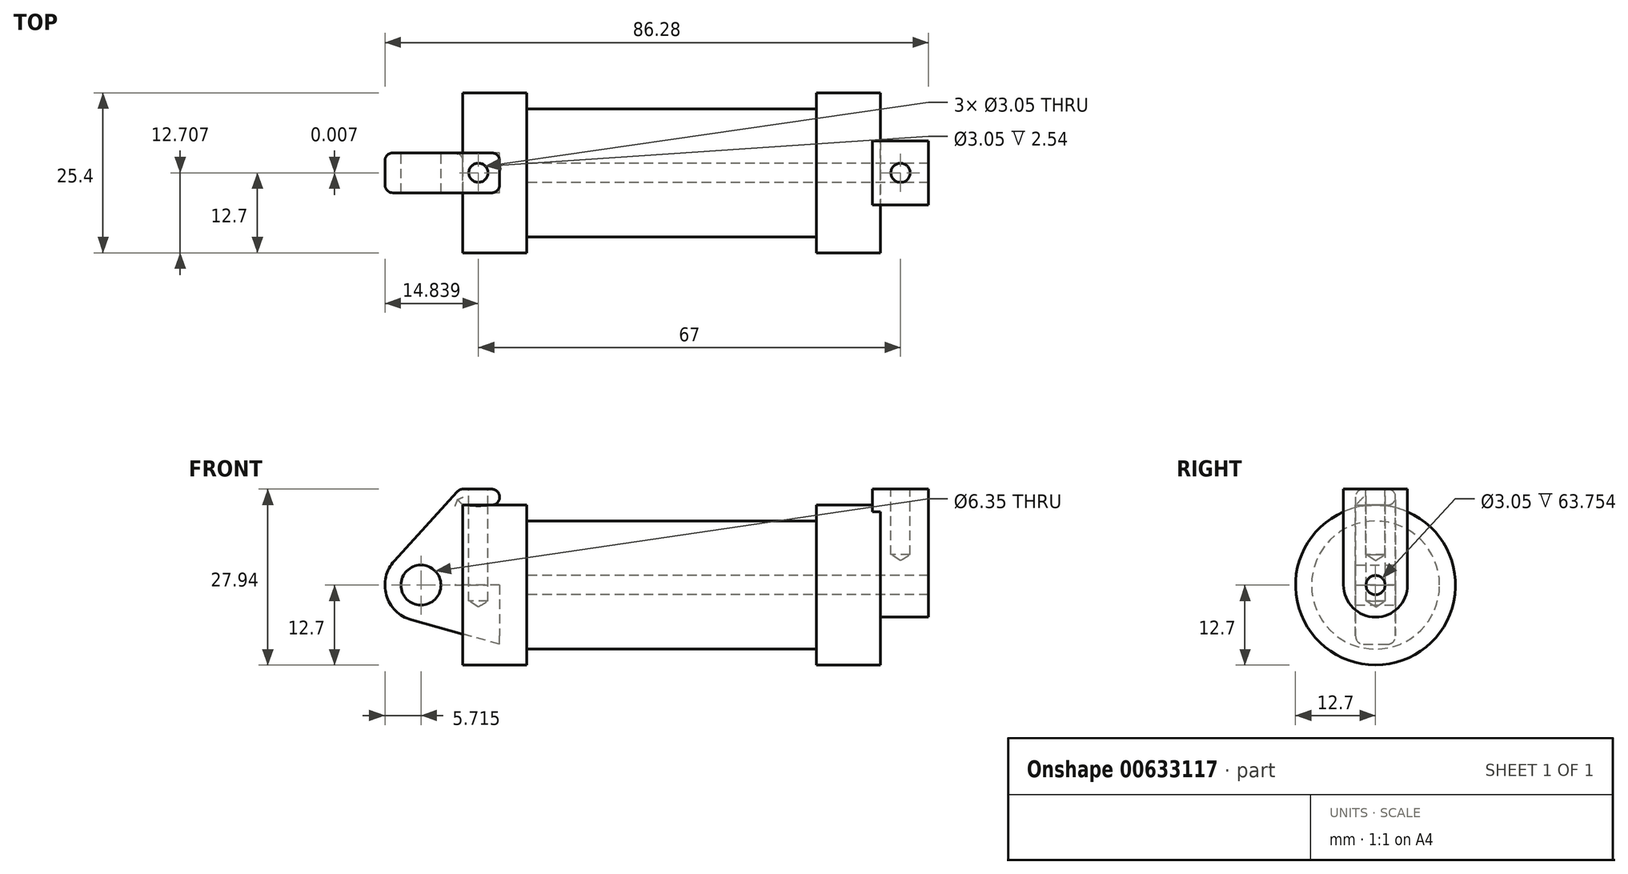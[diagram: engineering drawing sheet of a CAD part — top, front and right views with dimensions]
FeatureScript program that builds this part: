
annotation { "Feature Type Name" : "Feature", "Feature Type Description" : "" }
export const myFeature = defineFeature(function(context is Context, id is Id, definition is map)
    precondition{}
    {
        {
            var Q0;
            Q0=qCreatedBy(makeId("Front.planeOp"),FACE);
            var sketch = newSketch(context, id + "F0", { "sketchPlane" : qUnion([Q0])});
            skLineSegment(sketch, "E0", {"start": v(0, 0) * mm, "end": v(0, 12.7) * mm});
            skLineSegment(sketch, "E1", {"start": v(0, 12.7) * mm, "end": v(10.16, 12.7) * mm});
            skLineSegment(sketch, "E2", {"start": v(10.16, 12.7) * mm, "end": v(10.16, 10.16) * mm});
            skLineSegment(sketch, "E3", {"start": v(10.16, 10.16) * mm, "end": v(56.13, 10.16) * mm});
            skLineSegment(sketch, "E4", {"start": v(56.13, 10.16) * mm, "end": v(56.13, 12.7) * mm});
            skLineSegment(sketch, "E5", {"start": v(56.13, 12.7) * mm, "end": v(66.3, 12.7) * mm});
            skLineSegment(sketch, "E6", {"start": v(66.3, 12.7) * mm, "end": v(66.3, 0) * mm});
            skLineSegment(sketch, "E7", {"start": v(66.3, 0) * mm, "end": v(0, 0) * mm});
            skLineSegment(sketch, "E8", {"start": v(5.84, 15.24) * mm, "end": v(-0.5, 15.24) * mm});
            skLineSegment(sketch, "E9", {"start": v(-0.5, 15.24) * mm, "end": v(-10.88, 3.85) * mm});
            skLineSegment(sketch, "E10", {"start": v(0, 0) * mm, "end": v(-6.65, 0) * mm});
            skCircle(sketch, "E11", {"center": v(-6.65, 0) * mm, "radius": 5.72 * mm});
            skCircle(sketch, "E12", {"center": v(-6.65, 0) * mm, "radius": 3.18 * mm});
            skLineSegment(sketch, "E13", {"start": v(5.84, 15.24) * mm, "end": v(5.84, -9.4) * mm});
            skLineSegment(sketch, "E14", {"start": v(5.84, -9.4) * mm, "end": v(-8.18, -5.5) * mm});
            skSolve(sketch);
        }
        {
            var Q0;
            {var subQ0=sQuery(id+"F0.wireOp",EDGE,"E0");Q0=makeQuery(id+"F0.imprint","IMPRINT",FACE,{"disambiguationData":[TD([[makeQuery(id+"F0.imprint","IMPRINT",EDGE,{"derivedFrom":subQ0}),-1.0]])]});}
            var Q1;
            {var subQ0=sQuery(id+"F0.wireOp",EDGE,"E2");Q1=makeQuery(id+"F0.imprint","IMPRINT",FACE,{"disambiguationData":[TD([[makeQuery(id+"F0.imprint","IMPRINT",EDGE,{"derivedFrom":subQ0}),-1.0]])]});}
            var Q2;
            Q2=sQuery(id+"F0.wireOp",EDGE,"E7");
            revolve(context, id + "F1", {"entities" : qUnion([Q0, Q1]), "axis" : qUnion([Q2]), "revolveType" : RevolveType.FULL});
        }
        {
            var Q0;
            {var subQ0=sQuery(id+"F0.wireOp",EDGE,"E14");Q0=makeQuery(id+"F0.imprint","IMPRINT",FACE,{"disambiguationData":[TD([[makeQuery(id+"F0.imprint","IMPRINT",EDGE,{"derivedFrom":subQ0}),-1.0]])]});}
            var Q1;
            {var subQ1=sQuery(id+"F0.wireOp",EDGE,"E0");Q1=makeQuery(id+"F0.imprint","IMPRINT",FACE,{"disambiguationData":[TD([[makeQuery(id+"F0.imprint","IMPRINT",EDGE,{"derivedFrom":subQ1}),1.0]])]});}
            var Q2;
            {var subQ5=sQuery(id+"F0.wireOp",EDGE,"E12");Q2=makeQuery(id+"F0.imprint","IMPRINT",FACE,{"disambiguationData":[TD([[makeQuery(id+"F0.imprint","IMPRINT",EDGE,{"derivedFrom":subQ5}),-1.0]])]});}
            extrude(context, id + "F2", {"entities" : qUnion([Q0, Q1, Q2]), "endBound" : BoundingType.SYMMETRIC, "depth" : 6.35 * mm, "offsetDistance" : 25.4 * mm});
        }
        {
            var Q0;
            Q0=makeQuery(id+"F1.opRevolve","SWEPT_FACE",FACE,{"disambiguationData":[OSD([sQuery(id+"F0.wireOp",EDGE,"E6")])]});
            var sketch = newSketch(context, id + "F3", { "sketchPlane" : qUnion([Q0])});
            skCircle(sketch, "E15", {"center": v(0, 0) * mm, "radius": 1.52 * mm});
            skCircle(sketch, "E16", {"center": v(0, 0) * mm, "radius": 5.08 * mm});
            skLineSegment(sketch, "E17", {"start": v(-5.08, 0) * mm, "end": v(-5.08, 15.24) * mm});
            skLineSegment(sketch, "E18", {"start": v(5.08, 0) * mm, "end": v(5.08, 15.24) * mm});
            skLineSegment(sketch, "E19", {"start": v(5.08, 15.24) * mm, "end": v(-5.08, 15.24) * mm});
            skSolve(sketch);
        }
        {
            var Q0;
            Q0=makeQuery(id+"F3.imprint","IMPRINT",FACE,{"disambiguationData":[TD([[makeQuery(id+"F3.imprint","IMPRINT",EDGE,{"derivedFrom":sQuery(id+"F3.wireOp",EDGE,"E15")}),-1.0]])]});
            var Q1;
            {var subQ0=sQuery(id+"F3.wireOp",EDGE,"E17");var subQ1=sQuery(id+"F3.wireOp",EDGE,"E16");var subQ2=makeQuery(id+"F3.imprint","INTERSECT",VERTEX,{"derivedFrom":[subQ1,subQ0]});Q1=makeQuery(id+"F3.imprint","IMPRINT",FACE,{"disambiguationData":[TD([[makeQuery(id+"F3.imprint","IMPRINT",EDGE,{"disambiguationData":[TD([[subQ2,1.0]])],"derivedFrom":subQ1}),-1.0]])]});}
            var Q2;
            {var subQ0=sQuery(id+"F3.wireOp",EDGE,"E19");Q2=makeQuery(id+"F3.imprint","IMPRINT",FACE,{"disambiguationData":[TD([[makeQuery(id+"F3.imprint","IMPRINT",EDGE,{"derivedFrom":subQ0}),1.0]])]});}
            extrude(context, id + "F4", {"entities" : qUnion([Q0, Q1, Q2]), "operationType" : NewBodyOperationType.ADD, "depth" : 7.62 * mm, "offsetDistance" : 25.4 * mm, "hasSecondDirection" : true, "secondDirectionOppositeDirection" : true, "secondDirectionDepth" : 1.27 * mm});
        }
        {
            var Q0;
            Q0=makeQuery(id+"F4.boolean.opBoolean","SPLIT",FACE,{"disambiguationData":[TD([makeQuery(id+"F4.opExtrude","SWEPT_FACE",FACE,{"disambiguationData":[OSD([sQuery(id+"F3.wireOp",EDGE,"E15")])]})])],"derivedFrom":makeQuery(id+"F1.opRevolve","SWEPT_FACE",FACE,{"disambiguationData":[OSD([sQuery(id+"F0.wireOp",EDGE,"E6")])]})});
            var Q1;
            Q1=makeQuery(id+"F1.opRevolve","SWEPT_FACE",FACE,{"disambiguationData":[OSD([sQuery(id+"F0.wireOp",EDGE,"E2")])]});
            extrude(context, id + "F5", {"entities" : qUnion([Q0]), "operationType" : NewBodyOperationType.REMOVE, "endBound" : BoundingType.UP_TO_SURFACE, "oppositeDirection" : true, "depth" : 25.4 * mm, "endBoundEntityFace" : qUnion([Q1]), "offsetDistance" : 25.4 * mm});
        }
        {
            var Q0;
            Q0=makeQuery(id+"F4.opExtrude","SWEPT_FACE",FACE,{"disambiguationData":[OSD([sQuery(id+"F3.wireOp",EDGE,"E19")])]});
            var sketch = newSketch(context, id + "F6", { "sketchPlane" : qUnion([Q0])});
            skCircle(sketch, "E20", {"center": v(69.47, 0) * mm, "radius": 1.52 * mm});
            skPoint(sketch, "E20.centerSnap0", {"position": v(69.47, 5.08) * mm});
            skPoint(sketch, "E20.centerSnap1", {"position": v(65.02, 0) * mm});
            skSolve(sketch);
        }
        {
            var Q0;
            Q0=makeQuery(id+"F2.opExtrude","SWEPT_FACE",FACE,{"disambiguationData":[OSD([sQuery(id+"F0.wireOp",EDGE,"E8")])]});
            var sketch = newSketch(context, id + "F7", { "sketchPlane" : qUnion([Q0])});
            skCircle(sketch, "E21", {"center": v(2.47, 0) * mm, "radius": 1.52 * mm});
            skSolve(sketch);
        }
        {
            var Q0;
            Q0=sQuery(id+"F7.wireOp",VERTEX,"E21.center");
            var Q1;
            Q1=makeQuery(id+"F1.opRevolve","SWEPT_BODY",BODY,{"disambiguationData":[OSD([sQuery(id+"F0.wireOp",EDGE,"E0"),sQuery(id+"F0.wireOp",EDGE,"E1"),sQuery(id+"F0.wireOp",EDGE,"E2"),sQuery(id+"F0.wireOp",EDGE,"E3"),sQuery(id+"F0.wireOp",EDGE,"E4"),sQuery(id+"F0.wireOp",EDGE,"E5"),sQuery(id+"F0.wireOp",EDGE,"E6"),sQuery(id+"F0.wireOp",EDGE,"E7")])]});
            var Q2;
            Q2=makeQuery(id+"F2.opExtrude","SWEPT_BODY",BODY,{"disambiguationData":[OSD([sQuery(id+"F0.wireOp",EDGE,"E0"),sQuery(id+"F0.wireOp",EDGE,"E1"),sQuery(id+"F0.wireOp",EDGE,"E7"),sQuery(id+"F0.wireOp",EDGE,"E8"),sQuery(id+"F0.wireOp",EDGE,"E9"),sQuery(id+"F0.wireOp",EDGE,"E11"),sQuery(id+"F0.wireOp",EDGE,"E12"),sQuery(id+"F0.wireOp",EDGE,"E13"),sQuery(id+"F0.wireOp",EDGE,"E14")])]});
            hole(context, id + "F8", {"style" : HoleStyle.SIMPLE, "endStyle" : HoleEndStyle.BLIND, "holeDiameter" : 3.05 * mm, "majorDiameter" : 6.35 * mm, "holeDepth" : 17.78 * mm, "isTappedThrough" : true, "tappedDepth" : 12.7 * mm, "tapClearance" : 3, "locations" : qUnion([Q0]), "scope" : qUnion([Q1, Q2])});
        }
        {
            var Q0;
            Q0=sQuery(id+"F6.wireOp",VERTEX,"E20.center");
            var Q1;
            Q1=makeQuery(id+"F1.opRevolve","SWEPT_BODY",BODY,{"disambiguationData":[OSD([sQuery(id+"F0.wireOp",EDGE,"E0"),sQuery(id+"F0.wireOp",EDGE,"E1"),sQuery(id+"F0.wireOp",EDGE,"E2"),sQuery(id+"F0.wireOp",EDGE,"E3"),sQuery(id+"F0.wireOp",EDGE,"E4"),sQuery(id+"F0.wireOp",EDGE,"E5"),sQuery(id+"F0.wireOp",EDGE,"E6"),sQuery(id+"F0.wireOp",EDGE,"E7")])]});
            hole(context, id + "F9", {"style" : HoleStyle.SIMPLE, "endStyle" : HoleEndStyle.BLIND, "holeDiameter" : 3.05 * mm, "majorDiameter" : 6.35 * mm, "holeDepth" : 10.4 * mm, "isTappedThrough" : true, "tappedDepth" : 12.7 * mm, "tapClearance" : 3, "locations" : qUnion([Q0]), "scope" : qUnion([Q1])});
        }
        {
            var Q0;
            Q0=makeQuery(id+"F1.opRevolve","SWEPT_EDGE",EDGE,{"disambiguationData":[OSD([sQuery(id+"F0.wireOp",EDGE,"E1"),sQuery(id+"F0.wireOp",EDGE,"E2")])]});
            var Q1;
            Q1=makeQuery(id+"F1.opRevolve","SWEPT_EDGE",EDGE,{"disambiguationData":[OSD([sQuery(id+"F0.wireOp",EDGE,"E0"),sQuery(id+"F0.wireOp",EDGE,"E1")])]});
            var Q2;
            Q2=makeQuery(id+"F1.opRevolve","SWEPT_FACE",FACE,{"disambiguationData":[OSD([sQuery(id+"F0.wireOp",EDGE,"E5")])]});
            var Q3;
            Q3=makeQuery(id+"F4.opExtrude","SWEPT_EDGE",EDGE,{"disambiguationData":[OSD([sQuery(id+"F3.wireOp",EDGE,"E17"),sQuery(id+"F3.wireOp",EDGE,"E19")])]});
            var Q4;
            Q4=makeQuery(id+"F4.opExtrude","CAP_EDGE",EDGE,{"disambiguationData":[OSD([sQuery(id+"F3.wireOp",EDGE,"E19")])],"isStart":false});
            var Q5;
            Q5=makeQuery(id+"F4.opExtrude","SWEPT_EDGE",EDGE,{"disambiguationData":[OSD([sQuery(id+"F3.wireOp",EDGE,"E18"),sQuery(id+"F3.wireOp",EDGE,"E19")])]});
            var Q6;
            Q6=makeQuery(id+"F4.opExtrude","CAP_EDGE",EDGE,{"disambiguationData":[OSD([sQuery(id+"F3.wireOp",EDGE,"E19")])],"isStart":true});
            var Q7;
            Q7=makeQuery(id+"F4.opExtrude","CAP_EDGE",EDGE,{"disambiguationData":[OSD([sQuery(id+"F3.wireOp",EDGE,"E17")])],"isStart":true});
            var Q8;
            Q8=makeQuery(id+"F4.opExtrude","CAP_EDGE",EDGE,{"disambiguationData":[OSD([sQuery(id+"F3.wireOp",EDGE,"E18")])],"isStart":true});
            var Q9;
            Q9=makeQuery(id+"F4.opExtrude","CAP_EDGE",EDGE,{"disambiguationData":[OSD([sQuery(id+"F3.wireOp",EDGE,"E18")])],"isStart":false});
            var Q10;
            Q10=makeQuery(id+"F4.opExtrude","CAP_EDGE",EDGE,{"disambiguationData":[OSD([sQuery(id+"F3.wireOp",EDGE,"E16")])],"isStart":false});
            var Q11;
            Q11=makeQuery(id+"F4.opExtrude","CAP_EDGE",EDGE,{"disambiguationData":[OSD([sQuery(id+"F3.wireOp",EDGE,"E17")])],"isStart":false});
            var Q12;
            Q12=makeQuery(id+"F2.opExtrude","CAP_EDGE",EDGE,{"disambiguationData":[OSD([sQuery(id+"F0.wireOp",EDGE,"E8")])],"isStart":true});
            var Q13;
            Q13=makeQuery(id+"F2.opExtrude","SWEPT_EDGE",EDGE,{"disambiguationData":[OSD([sQuery(id+"F0.wireOp",EDGE,"E8"),sQuery(id+"F0.wireOp",EDGE,"E9")])]});
            var Q14;
            Q14=makeQuery(id+"F2.opExtrude","CAP_EDGE",EDGE,{"disambiguationData":[OSD([sQuery(id+"F0.wireOp",EDGE,"E8")])],"isStart":false});
            var Q15;
            Q15=makeQuery(id+"F2.opExtrude","SWEPT_EDGE",EDGE,{"disambiguationData":[OSD([sQuery(id+"F0.wireOp",EDGE,"E8"),sQuery(id+"F0.wireOp",EDGE,"E13")])]});
            var Q16;
            {var subQ0=sQuery(id+"F0.wireOp",EDGE,"E13");Q16=makeQuery(id+"F2.opExtrude","CAP_EDGE",EDGE,{"disambiguationData":[OSD([subQ0]),TDD([makeQuery(id+"F0.imprint","IMPRINT",EDGE,{"disambiguationData":[TD([[makeQuery(id+"F0.imprint","INTERSECT",VERTEX,{"derivedFrom":[sQuery(id+"F0.wireOp",EDGE,"E8"),subQ0]}),-1.0]])],"derivedFrom":subQ0})])],"isStart":true});}
            var Q17;
            {var subQ0=sQuery(id+"F0.wireOp",EDGE,"E13");Q17=makeQuery(id+"F2.opExtrude","CAP_EDGE",EDGE,{"disambiguationData":[OSD([subQ0]),TDD([makeQuery(id+"F0.imprint","IMPRINT",EDGE,{"disambiguationData":[TD([[makeQuery(id+"F0.imprint","INTERSECT",VERTEX,{"derivedFrom":[sQuery(id+"F0.wireOp",EDGE,"E8"),subQ0]}),-1.0]])],"derivedFrom":subQ0})])],"isStart":false});}
            var Q18;
            Q18=makeQuery(id+"F2.opExtrude","SWEPT_EDGE",EDGE,{"disambiguationData":[OSD([sQuery(id+"F0.wireOp",EDGE,"E1"),sQuery(id+"F0.wireOp",EDGE,"E13")])]});
            var Q19;
            Q19=makeQuery(id+"F2.opExtrude","CAP_EDGE",EDGE,{"disambiguationData":[OSD([sQuery(id+"F0.wireOp",EDGE,"E1")])],"isStart":true});
            var Q20;
            Q20=makeQuery(id+"F2.opExtrude","CAP_EDGE",EDGE,{"disambiguationData":[OSD([sQuery(id+"F0.wireOp",EDGE,"E9")])],"isStart":false});
            var Q21;
            Q21=makeQuery(id+"F2.opExtrude","CAP_EDGE",EDGE,{"disambiguationData":[OSD([sQuery(id+"F0.wireOp",EDGE,"E9")])],"isStart":true});
            var Q22;
            Q22=makeQuery(id+"F2.opExtrude","CAP_EDGE",EDGE,{"disambiguationData":[OSD([sQuery(id+"F0.wireOp",EDGE,"E11")])],"isStart":true});
            var Q23;
            Q23=makeQuery(id+"F2.opExtrude","CAP_EDGE",EDGE,{"disambiguationData":[OSD([sQuery(id+"F0.wireOp",EDGE,"E11")])],"isStart":false});
            var Q24;
            Q24=makeQuery(id+"F2.opExtrude","CAP_EDGE",EDGE,{"disambiguationData":[OSD([sQuery(id+"F0.wireOp",EDGE,"E14")])],"isStart":true});
            var Q25;
            Q25=makeQuery(id+"F2.opExtrude","CAP_EDGE",EDGE,{"disambiguationData":[OSD([sQuery(id+"F0.wireOp",EDGE,"E14")])],"isStart":false});
            var Q26;
            Q26=makeQuery(id+"F2.opExtrude","CAP_EDGE",EDGE,{"disambiguationData":[OSD([sQuery(id+"F0.wireOp",EDGE,"E0")])],"isStart":true});
            fillet(context, id + "F10", {"entities" : qUnion([Q0, Q1, Q2, Q3, Q4, Q5, Q6, Q7, Q8, Q9, Q10, Q11, Q12, Q13, Q14, Q15, Q16, Q17, Q18, Q19, Q20, Q21, Q22, Q23, Q24, Q25, Q26]), "radius" : 1.27 * mm, "tangentPropagation" : true, "allowEdgeOverflow" : false});
        }
    });
